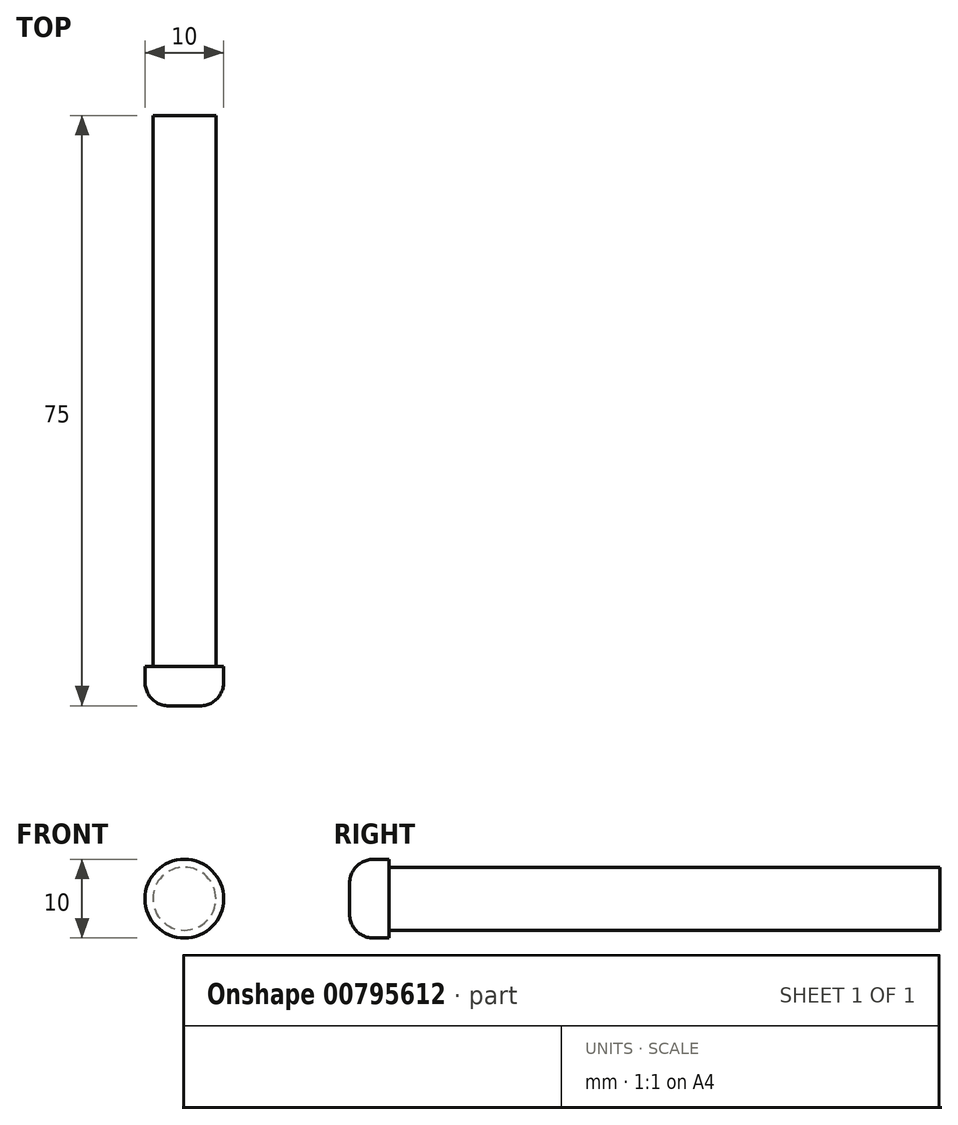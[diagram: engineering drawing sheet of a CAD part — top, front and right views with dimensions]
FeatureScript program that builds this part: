
annotation { "Feature Type Name" : "Feature", "Feature Type Description" : "" }
export const myFeature = defineFeature(function(context is Context, id is Id, definition is map)
    precondition{}
    {
        {
            var Q0;
            Q0=qCreatedBy(makeId("Front.planeOp"),FACE);
            var sketch = newSketch(context, id + "F0", { "sketchPlane" : qUnion([Q0])});
            skCircle(sketch, "E0", {"center": v(0, 0) * mm, "radius": 4 * mm});
            skSolve(sketch);
        }
        {
            var Q0;
            Q0=makeQuery(id+"F0.imprint","IMPRINT",FACE,{"disambiguationData":[TD([[makeQuery(id+"F0.imprint","IMPRINT",EDGE,{"derivedFrom":sQuery(id+"F0.wireOp",EDGE,"E0")}),1.0]])]});
            extrude(context, id + "F1", {"entities" : qUnion([Q0]), "endBound" : BoundingType.SYMMETRIC, "oppositeDirection" : true, "depth" : 70 * mm, "offsetDistance" : 25 * mm});
        }
        {
            var Q0;
            Q0=makeQuery(id+"F1.opExtrude","CAP_FACE",FACE,{"disambiguationData":[OSD([sQuery(id+"F0.wireOp",EDGE,"E0")])],"isStart":true});
            var sketch = newSketch(context, id + "F2", { "sketchPlane" : qUnion([Q0])});
            skCircle(sketch, "E1", {"center": v(0, 0) * mm, "radius": 5 * mm});
            skSolve(sketch);
        }
        {
            var Q0;
            Q0=makeQuery(id+"F2.imprint","IMPRINT",FACE,{"disambiguationData":[TD([[makeQuery(id+"F2.imprint","IMPRINT",EDGE,{"derivedFrom":sQuery(id+"F2.wireOp",EDGE,"E1")}),1.0]])]});
            var Q1;
            Q1=makeQuery(id+"F2.imprint","IMPRINT",FACE,{"disambiguationData":[TD([[makeQuery(id+"F2.imprint","IMPRINT",EDGE,{"derivedFrom":makeQuery(id+"F1.opExtrude","CAP_EDGE",EDGE,{"disambiguationData":[OSD([sQuery(id+"F0.wireOp",EDGE,"E0")])],"isStart":true})}),1.0]])]});
            extrude(context, id + "F3", {"entities" : qUnion([Q0, Q1]), "operationType" : NewBodyOperationType.ADD, "depth" : 5 * mm, "offsetDistance" : 25 * mm});
        }
        {
            var Q0;
            Q0=makeQuery(id+"F3.opExtrude","CAP_EDGE",EDGE,{"disambiguationData":[OSD([sQuery(id+"F2.wireOp",EDGE,"E1")])],"isStart":false});
            fillet(context, id + "F4", {"entities" : qUnion([Q0]), "radius" : 3 * mm, "tangentPropagation" : true, "allowEdgeOverflow" : false});
        }
    });
